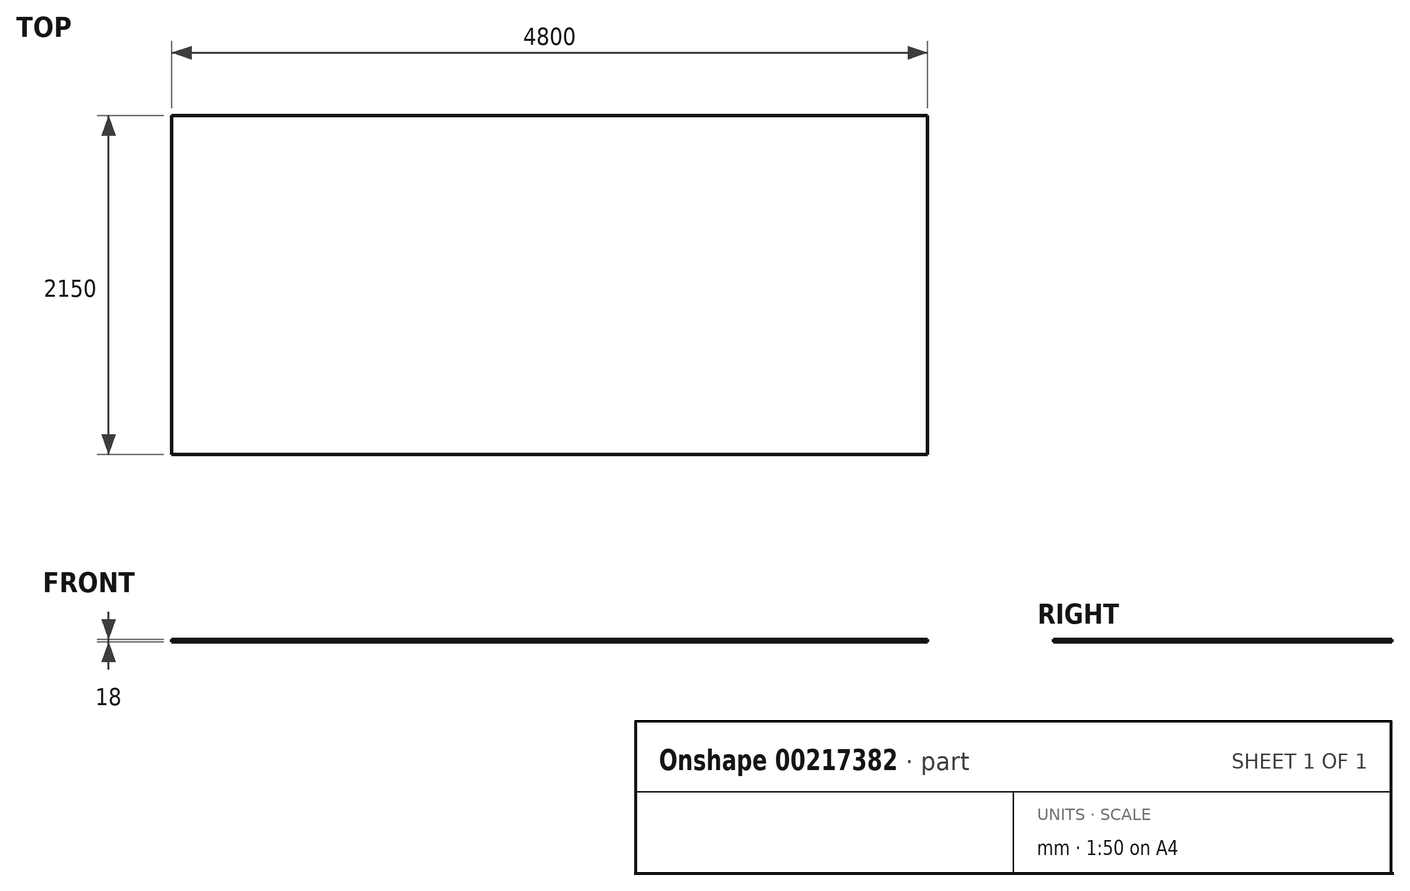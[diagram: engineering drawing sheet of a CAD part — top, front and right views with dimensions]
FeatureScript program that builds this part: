
annotation { "Feature Type Name" : "Feature", "Feature Type Description" : "" }
export const myFeature = defineFeature(function(context is Context, id is Id, definition is map)
    precondition{}
    {
        {
            var Q0;
            Q0=qCreatedBy(makeId("Top.planeOp"),FACE);
            var sketch = newSketch(context, id + "F0", { "sketchPlane" : qUnion([Q0])});
            skLineSegment(sketch, "E0.bottom", {"start": v(2400, 1075) * mm, "end": v(-2400, 1075) * mm});
            skLineSegment(sketch, "E0.top", {"start": v(2400, -1075) * mm, "end": v(-2400, -1075) * mm});
            skLineSegment(sketch, "E0.left", {"start": v(2400, 1075) * mm, "end": v(2400, -1075) * mm});
            skLineSegment(sketch, "E0.right", {"start": v(-2400, 1075) * mm, "end": v(-2400, -1075) * mm});
            skPoint(sketch, "E0.middle", {"position": v(0, 0) * mm});
            skSolve(sketch);
        }
        {
            var Q0;
            Q0=makeQuery(id+"F0.imprint","IMPRINT",FACE,{"disambiguationData":[TD([[makeQuery(id+"F0.imprint","IMPRINT",EDGE,{"derivedFrom":sQuery(id+"F0.wireOp",EDGE,"E0.bottom")}),1.0]])]});
            extrude(context, id + "F1", {"entities" : qUnion([Q0]), "depth" : 18 * mm});
        }
    });
